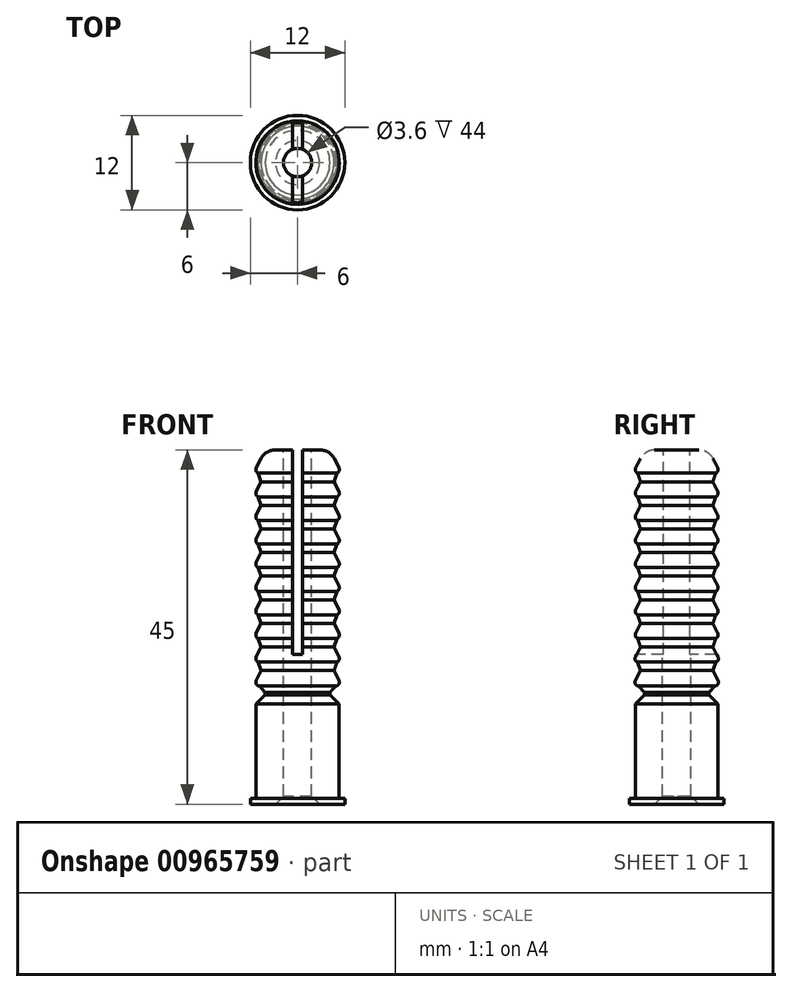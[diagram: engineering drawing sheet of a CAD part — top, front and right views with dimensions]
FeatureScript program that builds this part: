
annotation { "Feature Type Name" : "Feature", "Feature Type Description" : "" }
export const myFeature = defineFeature(function(context is Context, id is Id, definition is map)
    precondition{}
    {
        {
            var Q0;
            Q0=qCreatedBy(makeId("Front.planeOp"),FACE);
            var sketch = newSketch(context, id + "F0", { "sketchPlane" : qUnion([Q0])});
            skLineSegment(sketch, "E0", {"start": v(-4.66, 56) * mm, "end": v(-5.25, 54.84) * mm});
            skLineSegment(sketch, "E1", {"start": v(-4.8, 54.12) * mm, "end": v(-4.11, 54.12) * mm});
            skPoint(sketch, "E2.visualSharp", {"position": v(-5.61, 54.12) * mm});
            skArc(sketch, "E2.filletArc", {"start": v(-5.25, 54.84) * mm, "mid": v(-5.23, 54.35) * mm, "end": v(-4.8, 54.12) * mm});
            skLineSegment(sketch, "E3.1.0.0", {"start": v(-4.11, 54.12) * mm, "end": v(-5.25, 51.84) * mm});
            skLineSegment(sketch, "E3.1.0.1", {"start": v(-4.8, 51.12) * mm, "end": v(-4.11, 51.12) * mm});
            skArc(sketch, "E3.1.0.2", {"start": v(-5.25, 51.84) * mm, "mid": v(-5.23, 51.35) * mm, "end": v(-4.8, 51.12) * mm});
            skLineSegment(sketch, "E3.2.0.0", {"start": v(-4.11, 51.12) * mm, "end": v(-5.25, 48.84) * mm});
            skLineSegment(sketch, "E3.2.0.1", {"start": v(-4.8, 48.12) * mm, "end": v(-4.11, 48.12) * mm});
            skArc(sketch, "E3.2.0.2", {"start": v(-5.25, 48.84) * mm, "mid": v(-5.23, 48.35) * mm, "end": v(-4.8, 48.12) * mm});
            skLineSegment(sketch, "E3.3.0.0", {"start": v(-4.11, 48.12) * mm, "end": v(-5.25, 45.84) * mm});
            skLineSegment(sketch, "E3.3.0.1", {"start": v(-4.8, 45.12) * mm, "end": v(-4.11, 45.12) * mm});
            skArc(sketch, "E3.3.0.2", {"start": v(-5.25, 45.84) * mm, "mid": v(-5.23, 45.35) * mm, "end": v(-4.8, 45.12) * mm});
            skLineSegment(sketch, "E3.4.0.0", {"start": v(-4.11, 45.12) * mm, "end": v(-5.25, 42.84) * mm});
            skLineSegment(sketch, "E3.4.0.1", {"start": v(-4.8, 42.12) * mm, "end": v(-4.11, 42.12) * mm});
            skArc(sketch, "E3.4.0.2", {"start": v(-5.25, 42.84) * mm, "mid": v(-5.23, 42.35) * mm, "end": v(-4.8, 42.12) * mm});
            skLineSegment(sketch, "E3.5.0.0", {"start": v(-4.11, 42.12) * mm, "end": v(-5.25, 39.84) * mm});
            skLineSegment(sketch, "E3.5.0.1", {"start": v(-4.8, 39.12) * mm, "end": v(-4.11, 39.12) * mm});
            skArc(sketch, "E3.5.0.2", {"start": v(-5.25, 39.84) * mm, "mid": v(-5.23, 39.35) * mm, "end": v(-4.8, 39.12) * mm});
            skLineSegment(sketch, "E3.6.0.0", {"start": v(-4.11, 39.12) * mm, "end": v(-5.25, 36.84) * mm});
            skLineSegment(sketch, "E3.6.0.1", {"start": v(-4.8, 36.12) * mm, "end": v(-4.11, 36.12) * mm});
            skArc(sketch, "E3.6.0.2", {"start": v(-5.25, 36.84) * mm, "mid": v(-5.23, 36.35) * mm, "end": v(-4.8, 36.12) * mm});
            skLineSegment(sketch, "E3.7.0.0", {"start": v(-4.11, 36.12) * mm, "end": v(-5.25, 33.84) * mm});
            skLineSegment(sketch, "E3.7.0.1", {"start": v(-4.8, 33.12) * mm, "end": v(-4.11, 33.12) * mm});
            skArc(sketch, "E3.7.0.2", {"start": v(-5.25, 33.84) * mm, "mid": v(-5.23, 33.35) * mm, "end": v(-4.8, 33.12) * mm});
            skLineSegment(sketch, "E3.8.0.0", {"start": v(-4.11, 33.12) * mm, "end": v(-5.25, 30.84) * mm});
            skLineSegment(sketch, "E3.8.0.1", {"start": v(-4.8, 30.12) * mm, "end": v(-4.11, 30.12) * mm});
            skArc(sketch, "E3.8.0.2", {"start": v(-5.25, 30.84) * mm, "mid": v(-5.23, 30.35) * mm, "end": v(-4.8, 30.12) * mm});
            skLineSegment(sketch, "E3.direction1", {"start": v(-5.25, 54.84) * mm, "end": v(-5.25, 51.09) * mm, "construction": true});
            skLineSegment(sketch, "E4", {"start": v(-2.88, 57.12) * mm, "end": v(-1.8, 57.12) * mm});
            skLineSegment(sketch, "E5", {"start": v(-1.8, 57.12) * mm, "end": v(-1.8, 12.12) * mm});
            skLineSegment(sketch, "E6", {"start": v(-1.8, 12.12) * mm, "end": v(-6, 12.12) * mm});
            skLineSegment(sketch, "E7", {"start": v(-6, 12.12) * mm, "end": v(-6, 12.87) * mm});
            skLineSegment(sketch, "E8", {"start": v(-6, 12.87) * mm, "end": v(-5.25, 12.87) * mm});
            skLineSegment(sketch, "E9.0.9.0", {"start": v(-4.11, 30.12) * mm, "end": v(-5.25, 27.84) * mm});
            skLineSegment(sketch, "E9.3.9.0", {"start": v(-4.8, 27.12) * mm, "end": v(-4.11, 27.12) * mm});
            skArc(sketch, "E9.6.9.0", {"start": v(-5.25, 27.84) * mm, "mid": v(-5.23, 27.35) * mm, "end": v(-4.8, 27.12) * mm});
            skLineSegment(sketch, "E10", {"start": v(-4.11, 27.12) * mm, "end": v(-4.11, 26) * mm});
            skLineSegment(sketch, "E11", {"start": v(-4.11, 26) * mm, "end": v(-5.25, 24.87) * mm});
            skLineSegment(sketch, "E12", {"start": v(-5.25, 24.87) * mm, "end": v(-5.25, 12.87) * mm});
            skPoint(sketch, "E13.visualSharp", {"position": v(-4.11, 57.12) * mm});
            skArc(sketch, "E13.filletArc", {"start": v(-2.88, 57.12) * mm, "mid": v(-3.93, 56.82) * mm, "end": v(-4.66, 56) * mm});
            skSolve(sketch);
        }
        {
            var Q0;
            Q0=qCreatedBy(makeId("Front.planeOp"),FACE);
            var sketch = newSketch(context, id + "F1", { "sketchPlane" : qUnion([Q0])});
            skLineSegment(sketch, "E14", {"start": v(0, 62.43) * mm, "end": v(0, 10.7) * mm, "construction": true});
            skSolve(sketch);
        }
        {
            var Q0;
            Q0 = qSketchRegion(id + "F0", true);
            var Q1;
            Q1=sQuery(id+"F1.wireOp",EDGE,"E14");
            revolve(context, id + "F2", {"surfaceOperationType" : NewSurfaceOperationType.NEW, "entities" : qUnion([Q0]), "axis" : qUnion([Q1]), "revolveType" : RevolveType.FULL});
        }
        {
            var Q0;
            Q0=makeQuery(id+"F2.opRevolve","SWEPT_EDGE",EDGE,{"disambiguationData":[OSD([sQuery(id+"F0.wireOp",EDGE,"E1"),sQuery(id+"F0.wireOp",EDGE,"E3.1.0.0")])]});
            var Q1;
            Q1=makeQuery(id+"F2.opRevolve","SWEPT_EDGE",EDGE,{"disambiguationData":[OSD([sQuery(id+"F0.wireOp",EDGE,"E3.1.0.1"),sQuery(id+"F0.wireOp",EDGE,"E3.2.0.0")])]});
            var Q2;
            Q2=makeQuery(id+"F2.opRevolve","SWEPT_EDGE",EDGE,{"disambiguationData":[OSD([sQuery(id+"F0.wireOp",EDGE,"E3.2.0.1"),sQuery(id+"F0.wireOp",EDGE,"E3.3.0.0")])]});
            var Q3;
            Q3=makeQuery(id+"F2.opRevolve","SWEPT_EDGE",EDGE,{"disambiguationData":[OSD([sQuery(id+"F0.wireOp",EDGE,"E3.3.0.1"),sQuery(id+"F0.wireOp",EDGE,"E3.4.0.0")])]});
            var Q4;
            Q4=makeQuery(id+"F2.opRevolve","SWEPT_EDGE",EDGE,{"disambiguationData":[OSD([sQuery(id+"F0.wireOp",EDGE,"E3.4.0.1"),sQuery(id+"F0.wireOp",EDGE,"E3.5.0.0")])]});
            var Q5;
            Q5=makeQuery(id+"F2.opRevolve","SWEPT_EDGE",EDGE,{"disambiguationData":[OSD([sQuery(id+"F0.wireOp",EDGE,"E3.5.0.1"),sQuery(id+"F0.wireOp",EDGE,"E3.6.0.0")])]});
            var Q6;
            Q6=makeQuery(id+"F2.opRevolve","SWEPT_EDGE",EDGE,{"disambiguationData":[OSD([sQuery(id+"F0.wireOp",EDGE,"E3.6.0.1"),sQuery(id+"F0.wireOp",EDGE,"E3.7.0.0")])]});
            var Q7;
            Q7=makeQuery(id+"F2.opRevolve","SWEPT_EDGE",EDGE,{"disambiguationData":[OSD([sQuery(id+"F0.wireOp",EDGE,"E3.7.0.1"),sQuery(id+"F0.wireOp",EDGE,"E3.8.0.0")])]});
            var Q8;
            Q8=makeQuery(id+"F2.opRevolve","SWEPT_EDGE",EDGE,{"disambiguationData":[OSD([sQuery(id+"F0.wireOp",EDGE,"E3.8.0.1"),sQuery(id+"F0.wireOp",EDGE,"E9.0.9.0")])]});
            var Q9;
            Q9=makeQuery(id+"F2.opRevolve","SWEPT_EDGE",EDGE,{"disambiguationData":[OSD([sQuery(id+"F0.wireOp",EDGE,"E9.3.9.0"),sQuery(id+"F0.wireOp",EDGE,"E10")])]});
            chamfer(context, id + "F3", {"entities" : qUnion([Q0, Q1, Q2, Q3, Q4, Q5, Q6, Q7, Q8, Q9]), "width" : 0.8 * mm, "tangentPropagation" : true});
        }
        {
            var Q0;
            Q0=qCreatedBy(makeId("Front.planeOp"),FACE);
            var sketch = newSketch(context, id + "F4", { "sketchPlane" : qUnion([Q0])});
            skLineSegment(sketch, "E15", {"start": v(-0.65, 57.12) * mm, "end": v(-0.65, 31.12) * mm});
            skLineSegment(sketch, "E16", {"start": v(-0.65, 31.12) * mm, "end": v(0, 31.12) * mm});
            skLineSegment(sketch, "E17.MirrorCS", {"start": v(0.65, 57.12) * mm, "end": v(0.65, 31.12) * mm});
            skLineSegment(sketch, "E18", {"start": v(0, 31.12) * mm, "end": v(0.65, 31.12) * mm});
            skPoint(sketch, "E19.start.orphan", {"position": v(0, 57.12) * mm});
            skLineSegment(sketch, "E20", {"start": v(-0.65, 57.12) * mm, "end": v(0.65, 57.12) * mm});
            skSolve(sketch);
        }
        {
            var Q0;
            Q0 = qSketchRegion(id + "F4", true);
            extrude(context, id + "F5", {"entities" : qUnion([Q0]), "operationType" : NewBodyOperationType.REMOVE, "endBound" : BoundingType.SYMMETRIC, "oppositeDirection" : true, "depth" : 25 * mm, "offsetDistance" : 25 * mm});
        }
        {
            var Q0;
            Q0=makeQuery(id+"F2.opRevolve","SWEPT_EDGE",EDGE,{"disambiguationData":[OSD([sQuery(id+"F0.wireOp",EDGE,"E5"),sQuery(id+"F0.wireOp",EDGE,"E6")])]});
            chamfer(context, id + "F6", {"entities" : qUnion([Q0]), "width" : 1 * mm, "tangentPropagation" : true});
        }
    });
